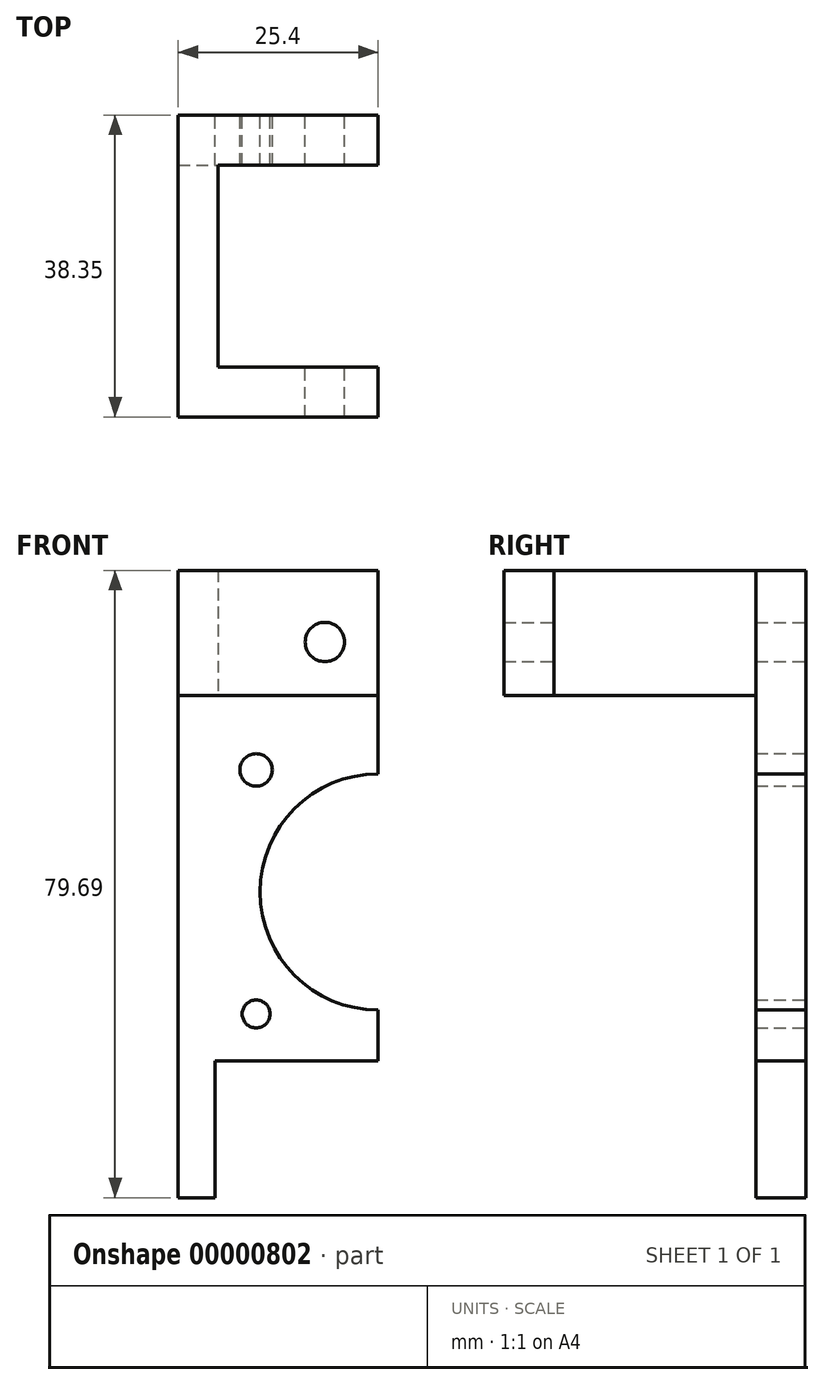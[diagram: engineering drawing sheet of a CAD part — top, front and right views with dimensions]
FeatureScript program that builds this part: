
annotation { "Feature Type Name" : "Feature", "Feature Type Description" : "" }
export const myFeature = defineFeature(function(context is Context, id is Id, definition is map)
    precondition{}
    {
        {
            var Q0;
            Q0=qCreatedBy(makeId("Front.planeOp"),FACE);
            var sketch = newSketch(context, id + "F0", { "sketchPlane" : qUnion([Q0])});
            skArc(sketch, "E0", {"start": v(0, 15) * mm, "mid": v(-15, 0) * mm, "end": v(0, -15) * mm});
            skCircle(sketch, "E1", {"center": v(-15.5, 15.5) * mm, "radius": 2.06 * mm});
            skCircle(sketch, "E2", {"center": v(-15.5, -15.5) * mm, "radius": 1.77 * mm});
            skLineSegment(sketch, "E3.rect.top", {"start": v(-20.74, -21.48) * mm, "end": v(0, -21.48) * mm});
            skLineSegment(sketch, "E3.rect.left", {"start": v(-25.4, 21.48) * mm, "end": v(-25.4, -21.48) * mm});
            skLineSegment(sketch, "E4", {"start": v(0, 21.48) * mm, "end": v(0, 15) * mm});
            skLineSegment(sketch, "E5.trimOffspring", {"start": v(0, -15) * mm, "end": v(0, -21.48) * mm});
            skLineSegment(sketch, "E6", {"start": v(0, 21.48) * mm, "end": v(0, 40.85) * mm});
            skLineSegment(sketch, "E7", {"start": v(0, 40.85) * mm, "end": v(-25.4, 40.85) * mm});
            skLineSegment(sketch, "E8", {"start": v(-25.4, 40.85) * mm, "end": v(-25.4, 21.48) * mm});
            skCircle(sketch, "E9", {"center": v(-6.77, 31.75) * mm, "radius": 2.5 * mm});
            skLineSegment(sketch, "E10", {"start": v(-25.4, -21.48) * mm, "end": v(-25.4, -38.84) * mm});
            skLineSegment(sketch, "E11", {"start": v(-25.4, -38.84) * mm, "end": v(-20.74, -38.84) * mm});
            skLineSegment(sketch, "E12", {"start": v(-20.74, -38.84) * mm, "end": v(-20.74, -21.48) * mm});
            skSolve(sketch);
        }
        {
            var Q0;
            Q0=makeQuery(id+"F0.imprint","IMPRINT",FACE,{"disambiguationData":[TD([[makeQuery(id+"F0.imprint","IMPRINT",EDGE,{"derivedFrom":sQuery(id+"F0.wireOp",EDGE,"E0")}),-1.0]])]});
            extrude(context, id + "F1", {"entities" : qUnion([Q0]), "depth" : 6.35 * mm});
        }
        {
            var Q0;
            Q0=makeQuery(id+"F1.opExtrude","CAP_FACE",FACE,{"disambiguationData":[OSD([sQuery(id+"F0.wireOp",EDGE,"E0"),sQuery(id+"F0.wireOp",EDGE,"E1"),sQuery(id+"F0.wireOp",EDGE,"E2"),sQuery(id+"F0.wireOp",EDGE,"E3.rect.top"),sQuery(id+"F0.wireOp",EDGE,"E4"),sQuery(id+"F0.wireOp",EDGE,"E5.trimOffspring"),sQuery(id+"F0.wireOp",EDGE,"E7"),sQuery(id+"F0.wireOp",EDGE,"E8"),sQuery(id+"F0.wireOp",EDGE,"E9"),sQuery(id+"F0.wireOp",EDGE,"E11"),sQuery(id+"F0.wireOp",EDGE,"E12")])],"isStart":false});
            var sketch = newSketch(context, id + "F2", { "sketchPlane" : qUnion([Q0])});
            skLineSegment(sketch, "E13.bottom", {"start": v(-25.4, 40.85) * mm, "end": v(-20.32, 40.85) * mm});
            skLineSegment(sketch, "E13.top", {"start": v(-25.4, 24.97) * mm, "end": v(-20.32, 24.97) * mm});
            skLineSegment(sketch, "E13.left", {"start": v(-25.4, 40.85) * mm, "end": v(-25.4, 24.97) * mm});
            skLineSegment(sketch, "E13.right", {"start": v(-20.32, 40.85) * mm, "end": v(-20.32, 24.97) * mm});
            skSolve(sketch);
        }
        {
            var Q0;
            Q0=makeQuery(id+"F2.imprint","IMPRINT",FACE,{"disambiguationData":[TD([[makeQuery(id+"F2.imprint","IMPRINT",EDGE,{"derivedFrom":sQuery(id+"F2.wireOp",EDGE,"E13.bottom")}),1.0]])]});
            extrude(context, id + "F3", {"entities" : qUnion([Q0]), "operationType" : NewBodyOperationType.ADD, "depth" : 25.65 * mm});
        }
        {
            var Q0;
            Q0=makeQuery(id+"F3.opExtrude","CAP_FACE",FACE,{"disambiguationData":[OSD([sQuery(id+"F2.wireOp",EDGE,"E13.bottom"),sQuery(id+"F2.wireOp",EDGE,"E13.top"),sQuery(id+"F2.wireOp",EDGE,"E13.left"),sQuery(id+"F2.wireOp",EDGE,"E13.right")])],"isStart":false});
            var sketch = newSketch(context, id + "F4", { "sketchPlane" : qUnion([Q0])});
            skLineSegment(sketch, "E14.bottom", {"start": v(-25.4, 40.85) * mm, "end": v(0, 40.85) * mm});
            skLineSegment(sketch, "E14.top", {"start": v(-25.4, 24.97) * mm, "end": v(0, 24.97) * mm});
            skLineSegment(sketch, "E14.left", {"start": v(-25.4, 40.85) * mm, "end": v(-25.4, 24.97) * mm});
            skLineSegment(sketch, "E14.right", {"start": v(0, 40.85) * mm, "end": v(0, 24.97) * mm});
            skCircle(sketch, "E15", {"center": v(-6.77, 31.75) * mm, "radius": 2.5 * mm});
            skSolve(sketch);
        }
        {
            var Q0;
            {var subQ2=sQuery(id+"F4.wireOp",EDGE,"E14.left");var subQ7=sQuery(id+"F4.wireOp",EDGE,"E14.right");Q0=qUnion([makeQuery(id+"F4.imprint","IMPRINT",FACE,{"disambiguationData":[TD([[makeQuery(id+"F4.imprint","IMPRINT",EDGE,{"derivedFrom":subQ2}),1.0]])]}),makeQuery(id+"F4.imprint","IMPRINT",FACE,{"disambiguationData":[TD([[makeQuery(id+"F4.imprint","IMPRINT",EDGE,{"derivedFrom":subQ7}),-1.0]])]})]);}
            extrude(context, id + "F5", {"entities" : qUnion([Q0]), "operationType" : NewBodyOperationType.ADD, "depth" : 6.35 * mm});
        }
    });
